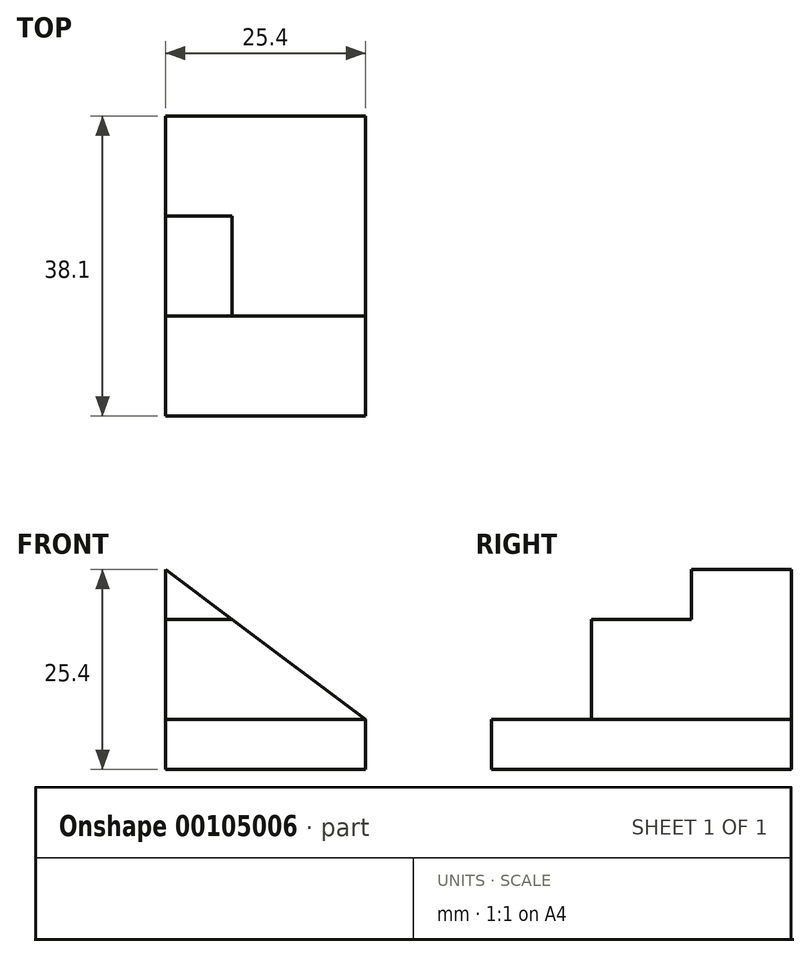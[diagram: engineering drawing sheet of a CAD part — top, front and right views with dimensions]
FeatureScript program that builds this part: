
annotation { "Feature Type Name" : "Feature", "Feature Type Description" : "" }
export const myFeature = defineFeature(function(context is Context, id is Id, definition is map)
    precondition{}
    {
        {
            var Q0;
            Q0=qCreatedBy(makeId("Front.planeOp"),FACE);
            var sketch = newSketch(context, id + "F0", { "sketchPlane" : qUnion([Q0])});
            skLineSegment(sketch, "E0.bottom", {"start": v(0, 0) * mm, "end": v(25.4, 0) * mm});
            skLineSegment(sketch, "E0.top", {"start": v(0, 6.35) * mm, "end": v(25.4, 6.35) * mm});
            skLineSegment(sketch, "E0.left", {"start": v(0, 0) * mm, "end": v(0, 6.35) * mm});
            skLineSegment(sketch, "E0.right", {"start": v(25.4, 0) * mm, "end": v(25.4, 6.35) * mm});
            skLineSegment(sketch, "E1", {"start": v(0, 6.35) * mm, "end": v(0, 25.4) * mm});
            skLineSegment(sketch, "E2", {"start": v(0, 25.4) * mm, "end": v(25.4, 6.35) * mm});
            skSolve(sketch);
        }
        {
            var Q0;
            Q0 = qSketchRegion(id + "F0", true);
            extrude(context, id + "F1", {"entities" : qUnion([Q0]), "oppositeDirection" : true, "depth" : 38.1 * mm});
        }
        {
            var Q0;
            Q0=makeQuery(id+"F1.opExtrude","SWEPT_FACE",FACE,{"disambiguationData":[OSD([sQuery(id+"F0.wireOp",EDGE,"E0.left"),sQuery(id+"F0.wireOp",EDGE,"E1")])]});
            var sketch = newSketch(context, id + "F2", { "sketchPlane" : qUnion([Q0])});
            skLineSegment(sketch, "E3.bottom", {"start": v(0, 25.4) * mm, "end": v(-12.7, 25.4) * mm});
            skLineSegment(sketch, "E3.top", {"start": v(0, 6.35) * mm, "end": v(-12.7, 6.35) * mm});
            skLineSegment(sketch, "E3.left", {"start": v(0, 25.4) * mm, "end": v(0, 6.35) * mm});
            skLineSegment(sketch, "E3.right", {"start": v(-12.7, 25.4) * mm, "end": v(-12.7, 6.35) * mm});
            skSolve(sketch);
        }
        {
            var Q0;
            Q0=makeQuery(id+"F2.imprint","IMPRINT",FACE,{"disambiguationData":[TD([[makeQuery(id+"F2.imprint","IMPRINT",EDGE,{"derivedFrom":sQuery(id+"F2.wireOp",EDGE,"E3.bottom")}),-1.0]])]});
            extrude(context, id + "F3", {"entities" : qUnion([Q0]), "operationType" : NewBodyOperationType.REMOVE, "oppositeDirection" : true, "depth" : 25.4 * mm});
        }
        {
            var Q0;
            Q0=makeQuery(id+"F3.boolean.opBoolean","COPY",FACE,{"derivedFrom":makeQuery(id+"F3.opExtrude","SWEPT_FACE",FACE,{"disambiguationData":[OSD([sQuery(id+"F2.wireOp",EDGE,"E3.right")])]})});
            var sketch = newSketch(context, id + "F4", { "sketchPlane" : qUnion([Q0])});
            skLineSegment(sketch, "E4", {"start": v(0, 19.05) * mm, "end": v(8.47, 19.05) * mm});
            skLineSegment(sketch, "E5", {"start": v(16.93, 12.7) * mm, "end": v(16.93, 6.35) * mm});
            skSolve(sketch);
        }
        {
            var Q0;
            {var subQ0=sQuery(id+"F4.wireOp",EDGE,"E4");Q0=makeQuery(id+"F4.imprint","IMPRINT",FACE,{"disambiguationData":[TD([[makeQuery(id+"F4.imprint","IMPRINT",EDGE,{"derivedFrom":subQ0}),1.0]])]});}
            extrude(context, id + "F5", {"entities" : qUnion([Q0]), "operationType" : NewBodyOperationType.REMOVE, "oppositeDirection" : true, "depth" : 12.7 * mm});
        }
    });
